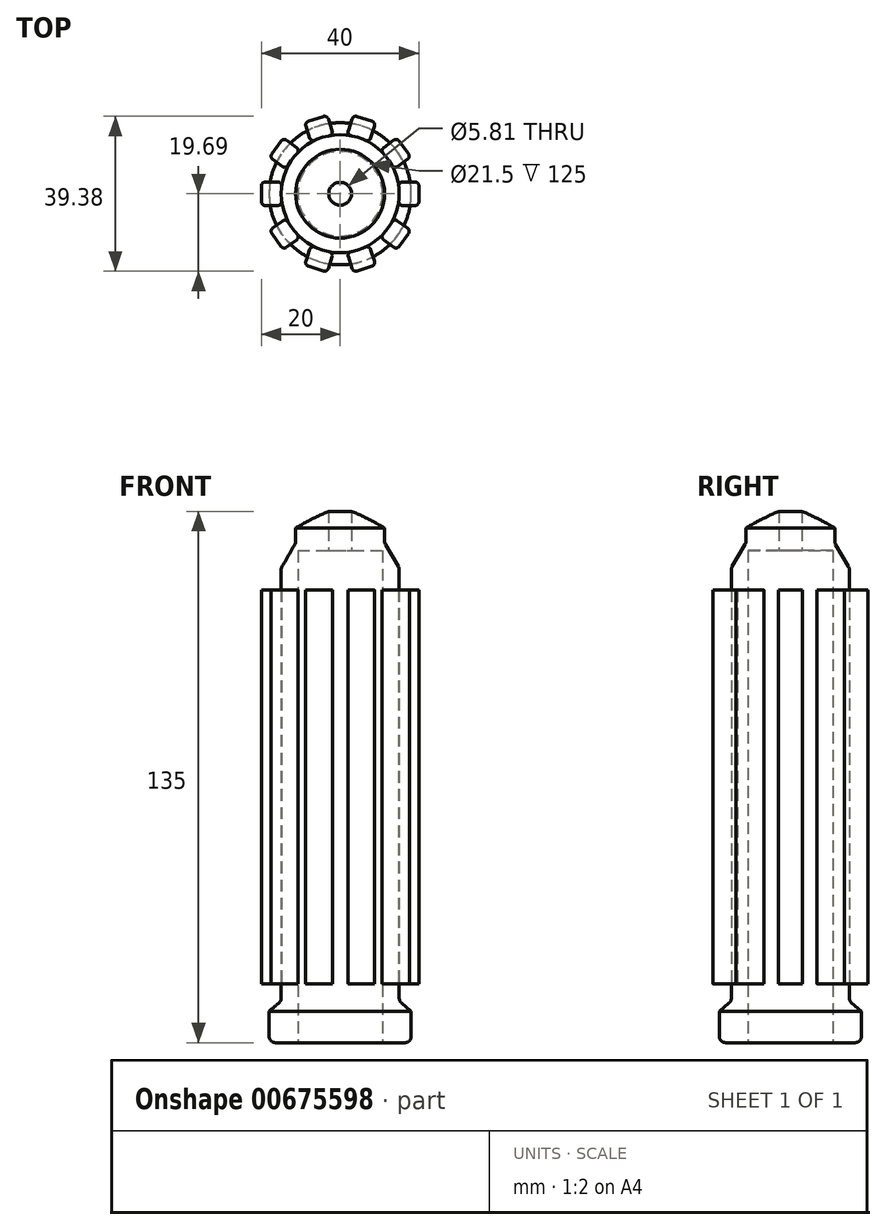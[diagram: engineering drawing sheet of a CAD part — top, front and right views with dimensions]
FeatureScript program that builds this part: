
annotation { "Feature Type Name" : "Feature", "Feature Type Description" : "" }
export const myFeature = defineFeature(function(context is Context, id is Id, definition is map)
    precondition{}
    {
        {
            var Q0;
            Q0=qCreatedBy(makeId("Front.planeOp"),FACE);
            var sketch = newSketch(context, id + "F0", { "sketchPlane" : qUnion([Q0])});
            skLineSegment(sketch, "E0", {"start": v(2.9, 135) * mm, "end": v(2.9, 125) * mm});
            skLineSegment(sketch, "E1", {"start": v(2.9, 125) * mm, "end": v(10.75, 125) * mm});
            skLineSegment(sketch, "E2", {"start": v(10.75, 125) * mm, "end": v(10.75, 0) * mm});
            skLineSegment(sketch, "E3", {"start": v(10.75, 0) * mm, "end": v(18.05, 0) * mm});
            skLineSegment(sketch, "E4", {"start": v(18.05, 0) * mm, "end": v(18.05, 8) * mm});
            skLineSegment(sketch, "E5", {"start": v(18.05, 8) * mm, "end": v(15, 10.56) * mm});
            skLineSegment(sketch, "E6", {"start": v(15, 10.56) * mm, "end": v(15, 120.56) * mm});
            skLineSegment(sketch, "E7", {"start": v(15, 120.56) * mm, "end": v(11.28, 127) * mm});
            skLineSegment(sketch, "E8", {"start": v(11.28, 127) * mm, "end": v(11.28, 130.75) * mm});
            skArc(sketch, "E9", {"start": v(11.28, 130.75) * mm, "mid": v(7.17, 133.02) * mm, "end": v(2.9, 135) * mm});
            skLineSegment(sketch, "E10", {"start": v(0, 0) * mm, "end": v(0, 74.22) * mm, "construction": true});
            skSolve(sketch);
        }
        {
            var Q0;
            Q0 = qSketchRegion(id + "F0", true);
            var Q1;
            Q1=sQuery(id+"F0.wireOp",EDGE,"E10");
            revolve(context, id + "F1", {"surfaceOperationType" : NewSurfaceOperationType.NEW, "entities" : qUnion([Q0]), "axis" : qUnion([Q1]), "revolveType" : RevolveType.FULL});
        }
        {
            var Q0;
            Q0=makeQuery(id+"F1.opRevolve","SWEPT_EDGE",EDGE,{"disambiguationData":[OSD([sQuery(id+"F0.wireOp",EDGE,"E6"),sQuery(id+"F0.wireOp",EDGE,"E7")])]});
            var Q1;
            Q1=makeQuery(id+"F1.opRevolve","SWEPT_EDGE",EDGE,{"disambiguationData":[OSD([sQuery(id+"F0.wireOp",EDGE,"E7"),sQuery(id+"F0.wireOp",EDGE,"E8")])]});
            var Q2;
            Q2=makeQuery(id+"F1.opRevolve","SWEPT_EDGE",EDGE,{"disambiguationData":[OSD([sQuery(id+"F0.wireOp",EDGE,"E3"),sQuery(id+"F0.wireOp",EDGE,"E4")])]});
            var Q3;
            Q3=makeQuery(id+"F1.opRevolve","SWEPT_EDGE",EDGE,{"disambiguationData":[OSD([sQuery(id+"F0.wireOp",EDGE,"E5"),sQuery(id+"F0.wireOp",EDGE,"E6")])]});
            fillet(context, id + "F2", {"entities" : qUnion([Q0, Q1, Q2, Q3]), "radius" : 1.6 * mm, "tangentPropagation" : true, "allowEdgeOverflow" : false});
        }
        {
            var Q0;
            Q0=qCreatedBy(makeId("Right.planeOp"),FACE);
            cPlane(context, id + "F3", {"entities" : qUnion([Q0]), "cplaneType" : CPlaneType.OFFSET, "offset" : 20 * mm, "width" : 150 * mm, "height" : 150 * mm});
        }
        {
            var Q0;
            Q0=qCreatedBy(id+"F3.planeOp",FACE);
            var sketch = newSketch(context, id + "F4", { "sketchPlane" : qUnion([Q0])});
            skLineSegment(sketch, "E11.bottom", {"start": v(-3, 115) * mm, "end": v(3, 115) * mm});
            skLineSegment(sketch, "E11.top", {"start": v(-3, 15) * mm, "end": v(3, 15) * mm});
            skLineSegment(sketch, "E11.left", {"start": v(-3, 115) * mm, "end": v(-3, 15) * mm});
            skLineSegment(sketch, "E11.right", {"start": v(3, 115) * mm, "end": v(3, 15) * mm});
            skSolve(sketch);
        }
        {
            var Q0;
            Q0 = qSketchRegion(id + "F4", true);
            var Q1;
            Q1=makeQuery(id+"F1.opRevolve","SWEPT_FACE",FACE,{"disambiguationData":[OSD([sQuery(id+"F0.wireOp",EDGE,"E6")])]});
            extrude(context, id + "F5", {"entities" : qUnion([Q0]), "endBound" : BoundingType.UP_TO_SURFACE, "oppositeDirection" : true, "depth" : 25 * mm, "endBoundEntityFace" : qUnion([Q1]), "offsetDistance" : 25 * mm});
        }
        {
            var Q0;
            Q0=makeQuery(id+"F5.opExtrude","CAP_EDGE",EDGE,{"disambiguationData":[OSD([sQuery(id+"F4.wireOp",EDGE,"E11.left")])],"isStart":true});
            var Q1;
            Q1=makeQuery(id+"F5.opExtrude","CAP_EDGE",EDGE,{"disambiguationData":[OSD([sQuery(id+"F4.wireOp",EDGE,"E11.right")])],"isStart":true});
            var Q2;
            Q2=makeQuery(id+"F5.opExtrude","CAP_EDGE",EDGE,{"disambiguationData":[OSD([sQuery(id+"F4.wireOp",EDGE,"E11.right")])],"isStart":false});
            var Q3;
            Q3=makeQuery(id+"F5.opExtrude","CAP_EDGE",EDGE,{"disambiguationData":[OSD([sQuery(id+"F4.wireOp",EDGE,"E11.left")])],"isStart":false});
            fillet(context, id + "F6", {"entities" : qUnion([Q0, Q1, Q2, Q3]), "radius" : 1 * mm, "tangentPropagation" : true, "allowEdgeOverflow" : false});
        }
        {
            var Q0;
            Q0=makeQuery(id+"F5.opExtrude","SWEPT_BODY",BODY,{"disambiguationData":[OSD([sQuery(id+"F4.wireOp",EDGE,"E11.bottom"),sQuery(id+"F4.wireOp",EDGE,"E11.top"),sQuery(id+"F4.wireOp",EDGE,"E11.left"),sQuery(id+"F4.wireOp",EDGE,"E11.right")])]});
            var Q1;
            Q1=makeQuery(id+"F1.opRevolve","SWEPT_FACE",FACE,{"disambiguationData":[OSD([sQuery(id+"F0.wireOp",EDGE,"E6")])]});
            circularPattern(context, id + "F7", {"entities" : qUnion([Q0]), "axis" : qUnion([Q1]), "angle" : 360 * degree, "instanceCount" : 10, "oppositeDirection" : true, "equalSpace" : true});
        }
    });
